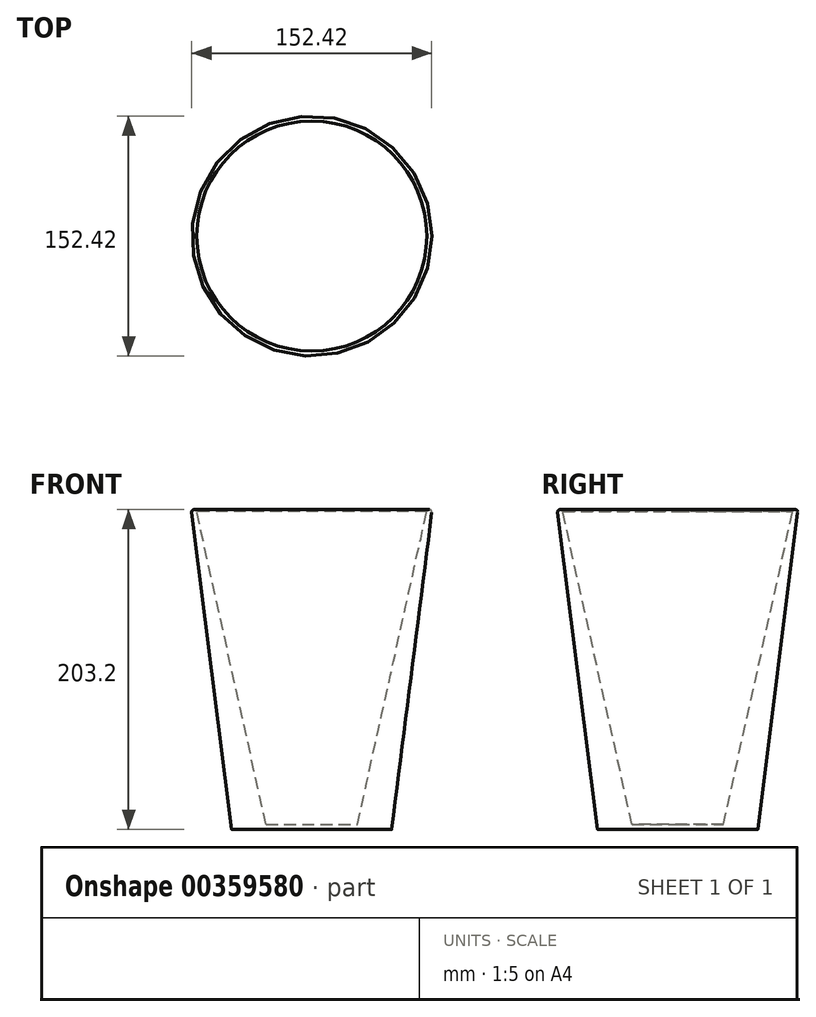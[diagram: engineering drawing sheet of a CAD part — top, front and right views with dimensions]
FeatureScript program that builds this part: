
annotation { "Feature Type Name" : "Feature", "Feature Type Description" : "" }
export const myFeature = defineFeature(function(context is Context, id is Id, definition is map)
    precondition{}
    {
        {
            assignVariable(context, id + "F0", {"name" : "thick", "anyValue" : .125});
        }
        {
            var Q0;
            Q0=qCreatedBy(makeId("Front.planeOp"),FACE);
            var sketch = newSketch(context, id + "F1", { "sketchPlane" : qUnion([Q0])});
            skLineSegment(sketch, "E0", {"start": v(0, 0) * mm, "end": v(-50.8, 0) * mm});
            skLineSegment(sketch, "E1", {"start": v(-50.8, 0) * mm, "end": v(-76.2, 201.41) * mm});
            skLineSegment(sketch, "E2", {"start": v(-73.06, 201.85) * mm, "end": v(-29.02, 3.17) * mm});
            skLineSegment(sketch, "E3", {"start": v(-29.02, 3.17) * mm, "end": v(0, 3.18) * mm});
            skLineSegment(sketch, "E4", {"start": v(0, 3.18) * mm, "end": v(0, 0) * mm});
            skArc(sketch, "E5", {"start": v(-76.2, 201.41) * mm, "mid": v(-74.84, 203.19) * mm, "end": v(-73.06, 201.85) * mm});
            skSolve(sketch);
        }
        {
            var Q0;
            Q0=makeQuery(id+"F1.imprint","IMPRINT",FACE,{"disambiguationData":[TD([[makeQuery(id+"F1.imprint","IMPRINT",EDGE,{"derivedFrom":sQuery(id+"F1.wireOp",EDGE,"E0")}),-1.0]])]});
            var Q1;
            Q1=sQuery(id+"F1.wireOp",EDGE,"E4");
            revolve(context, id + "F2", {"entities" : qUnion([Q0]), "axis" : qUnion([Q1]), "revolveType" : RevolveType.FULL});
        }
        {
            var Q0;
            Q0=makeQuery(id+"F2.opRevolve","SWEPT_EDGE",EDGE,{"disambiguationData":[OSD([sQuery(id+"F1.wireOp",EDGE,"E0"),sQuery(id+"F1.wireOp",EDGE,"E1")])]});
            var Q1;
            Q1=makeQuery(id+"F2.opRevolve","SWEPT_EDGE",EDGE,{"disambiguationData":[OSD([sQuery(id+"F1.wireOp",EDGE,"E2"),sQuery(id+"F1.wireOp",EDGE,"E3")])]});
            fillet(context, id + "F3", {"entities" : qUnion([Q0, Q1]), "radius" : (getVariable(context, 'thick') / 2) * mm, "tangentPropagation" : true, "allowEdgeOverflow" : false});
        }
    });
